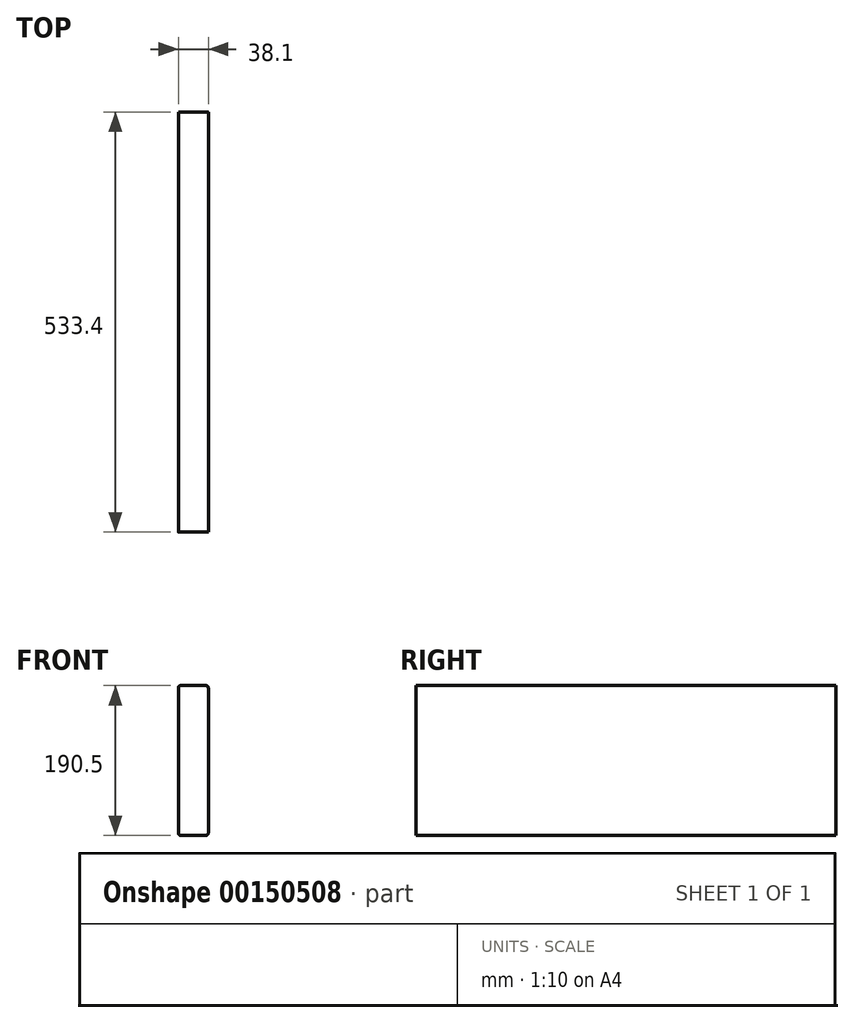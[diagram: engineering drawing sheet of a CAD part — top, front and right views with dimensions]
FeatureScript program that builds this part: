
annotation { "Feature Type Name" : "Feature", "Feature Type Description" : "" }
export const myFeature = defineFeature(function(context is Context, id is Id, definition is map)
    precondition{}
    {
        {
            var Q0;
            Q0=qCreatedBy(makeId("Right.planeOp"),FACE);
            var sketch = newSketch(context, id + "F0", { "sketchPlane" : qUnion([Q0])});
            skLineSegment(sketch, "E0.bottom", {"start": v(266.7, -95.25) * mm, "end": v(-266.7, -95.25) * mm});
            skLineSegment(sketch, "E0.top", {"start": v(266.7, 95.25) * mm, "end": v(-266.7, 95.25) * mm});
            skLineSegment(sketch, "E0.left", {"start": v(266.7, -95.25) * mm, "end": v(266.7, 95.25) * mm});
            skLineSegment(sketch, "E0.right", {"start": v(-266.7, -95.25) * mm, "end": v(-266.7, 95.25) * mm});
            skPoint(sketch, "E0.middle", {"position": v(0, 0) * mm});
            skSolve(sketch);
        }
        {
            var Q0;
            Q0=makeQuery(id+"F0.imprint","IMPRINT",FACE,{"disambiguationData":[TD([[makeQuery(id+"F0.imprint","IMPRINT",EDGE,{"derivedFrom":sQuery(id+"F0.wireOp",EDGE,"E0.bottom")}),-1.0]])]});
            extrude(context, id + "F1", {"entities" : qUnion([Q0]), "depth" : 38.1 * mm});
        }
        {
            var Q0;
            Q0=makeQuery(id+"F1.opExtrude","CAP_EDGE",EDGE,{"disambiguationData":[OSD([sQuery(id+"F0.wireOp",EDGE,"E0.top")])],"isStart":true});
            var Q1;
            Q1=makeQuery(id+"F1.opExtrude","CAP_EDGE",EDGE,{"disambiguationData":[OSD([sQuery(id+"F0.wireOp",EDGE,"E0.top")])],"isStart":false});
            var Q2;
            Q2=makeQuery(id+"F1.opExtrude","CAP_EDGE",EDGE,{"disambiguationData":[OSD([sQuery(id+"F0.wireOp",EDGE,"E0.bottom")])],"isStart":true});
            var Q3;
            Q3=makeQuery(id+"F1.opExtrude","CAP_EDGE",EDGE,{"disambiguationData":[OSD([sQuery(id+"F0.wireOp",EDGE,"E0.bottom")])],"isStart":false});
            fillet(context, id + "F2", {"entities" : qUnion([Q0, Q1, Q2, Q3]), "radius" : 3.17 * mm, "tangentPropagation" : true, "allowEdgeOverflow" : false});
        }
    });
